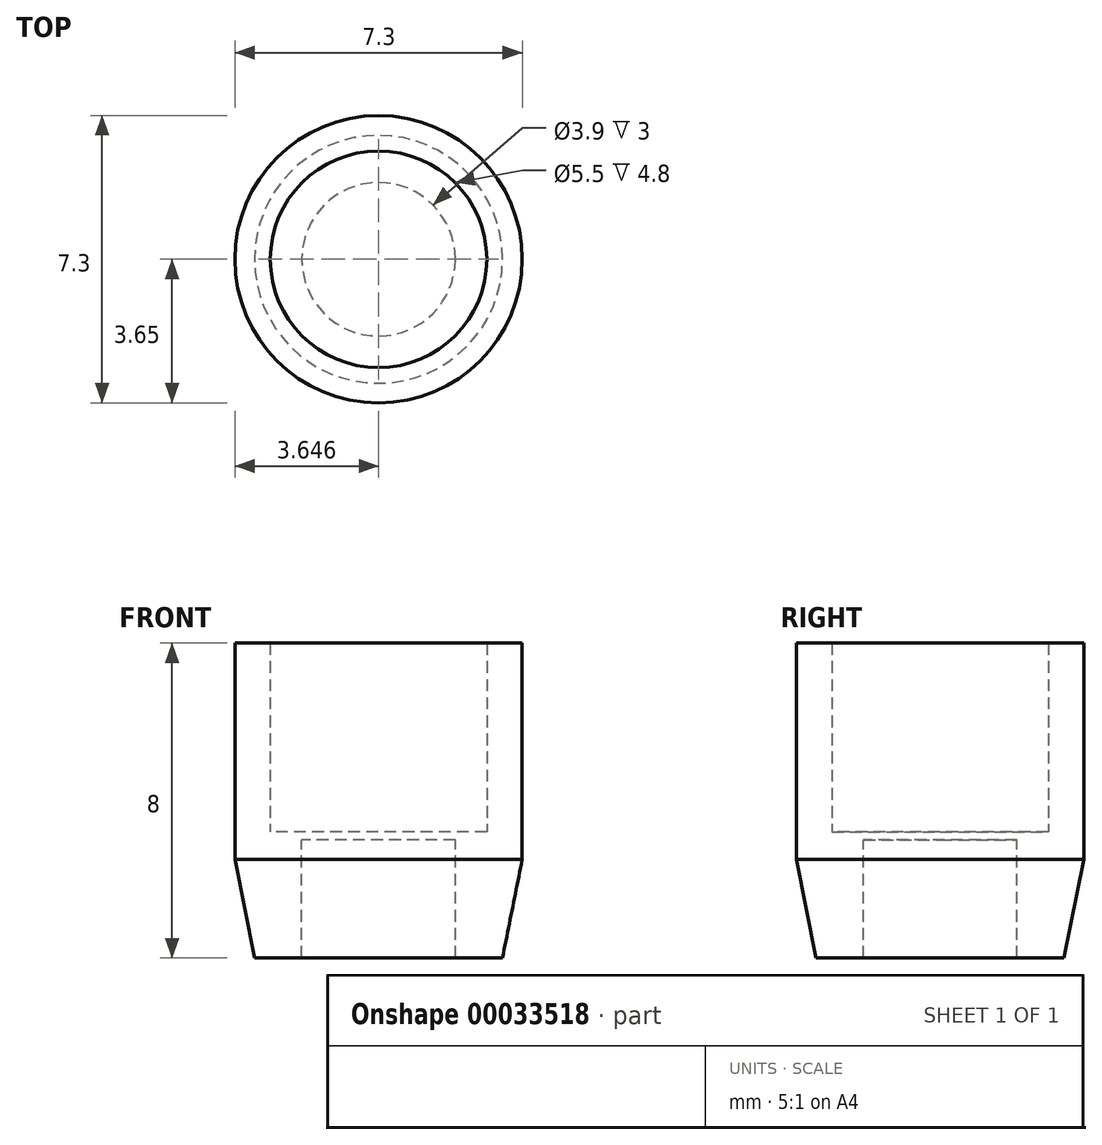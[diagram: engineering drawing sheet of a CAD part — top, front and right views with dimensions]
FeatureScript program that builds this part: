
annotation { "Feature Type Name" : "Feature", "Feature Type Description" : "" }
export const myFeature = defineFeature(function(context is Context, id is Id, definition is map)
    precondition{}
    {
        {
            var Q0;
            Q0=qCreatedBy(makeId("Top.planeOp"),FACE);
            var sketch = newSketch(context, id + "F0", { "sketchPlane" : qUnion([Q0])});
            skCircle(sketch, "E0", {"center": v(-17.5, 0) * mm, "radius": 1.95 * mm});
            skCircle(sketch, "E1", {"center": v(-17.5, 0) * mm, "radius": 2.75 * mm});
            skCircle(sketch, "E2.0", {"center": v(-17.5, 0) * mm, "radius": 3.65 * mm});
            skSolve(sketch);
        }
        {
            var Q0;
            Q0=makeQuery(id+"F0.imprint","IMPRINT",FACE,{"disambiguationData":[TD([[makeQuery(id+"F0.imprint","IMPRINT",EDGE,{"derivedFrom":sQuery(id+"F0.wireOp",EDGE,"E1")}),-1.0]])]});
            var Q1;
            Q1=makeQuery(id+"F0.imprint","IMPRINT",FACE,{"disambiguationData":[TD([[makeQuery(id+"F0.imprint","IMPRINT",EDGE,{"derivedFrom":sQuery(id+"F0.wireOp",EDGE,"E0")}),-1.0]])]});
            extrude(context, id + "F1", {"entities" : qUnion([Q0, Q1]), "oppositeDirection" : true, "depth" : 3 * mm});
        }
        {
            var Q0;
            Q0=makeQuery(id+"F0.imprint","IMPRINT",FACE,{"disambiguationData":[TD([[makeQuery(id+"F0.imprint","IMPRINT",EDGE,{"derivedFrom":sQuery(id+"F0.wireOp",EDGE,"E1")}),-1.0]])]});
            extrude(context, id + "F2", {"entities" : qUnion([Q0]), "operationType" : NewBodyOperationType.ADD, "depth" : 5 * mm});
        }
        {
            var Q0;
            Q0=makeQuery(id+"F1.opExtrude","CAP_EDGE",EDGE,{"disambiguationData":[OSD([sQuery(id+"F0.wireOp",EDGE,"E2.0")])],"isStart":false});
            chamfer(context, id + "F3", {"entities" : qUnion([Q0]), "chamferType" : ChamferType.TWO_OFFSETS, "width1" : 0.5 * mm, "oppositeDirection" : true, "width2" : 2.5 * mm, "tangentPropagation" : true});
        }
        {
            var Q0;
            Q0=makeQuery(id+"F0.imprint","IMPRINT",FACE,{"disambiguationData":[TD([[makeQuery(id+"F0.imprint","IMPRINT",EDGE,{"derivedFrom":sQuery(id+"F0.wireOp",EDGE,"E0")}),1.0]])]});
            var Q1;
            Q1=makeQuery(id+"F0.imprint","IMPRINT",FACE,{"disambiguationData":[TD([[makeQuery(id+"F0.imprint","IMPRINT",EDGE,{"derivedFrom":sQuery(id+"F0.wireOp",EDGE,"E0")}),-1.0]])]});
            extrude(context, id + "F4", {"entities" : qUnion([Q0, Q1]), "operationType" : NewBodyOperationType.ADD, "depth" : 0.2 * mm});
        }
    });
